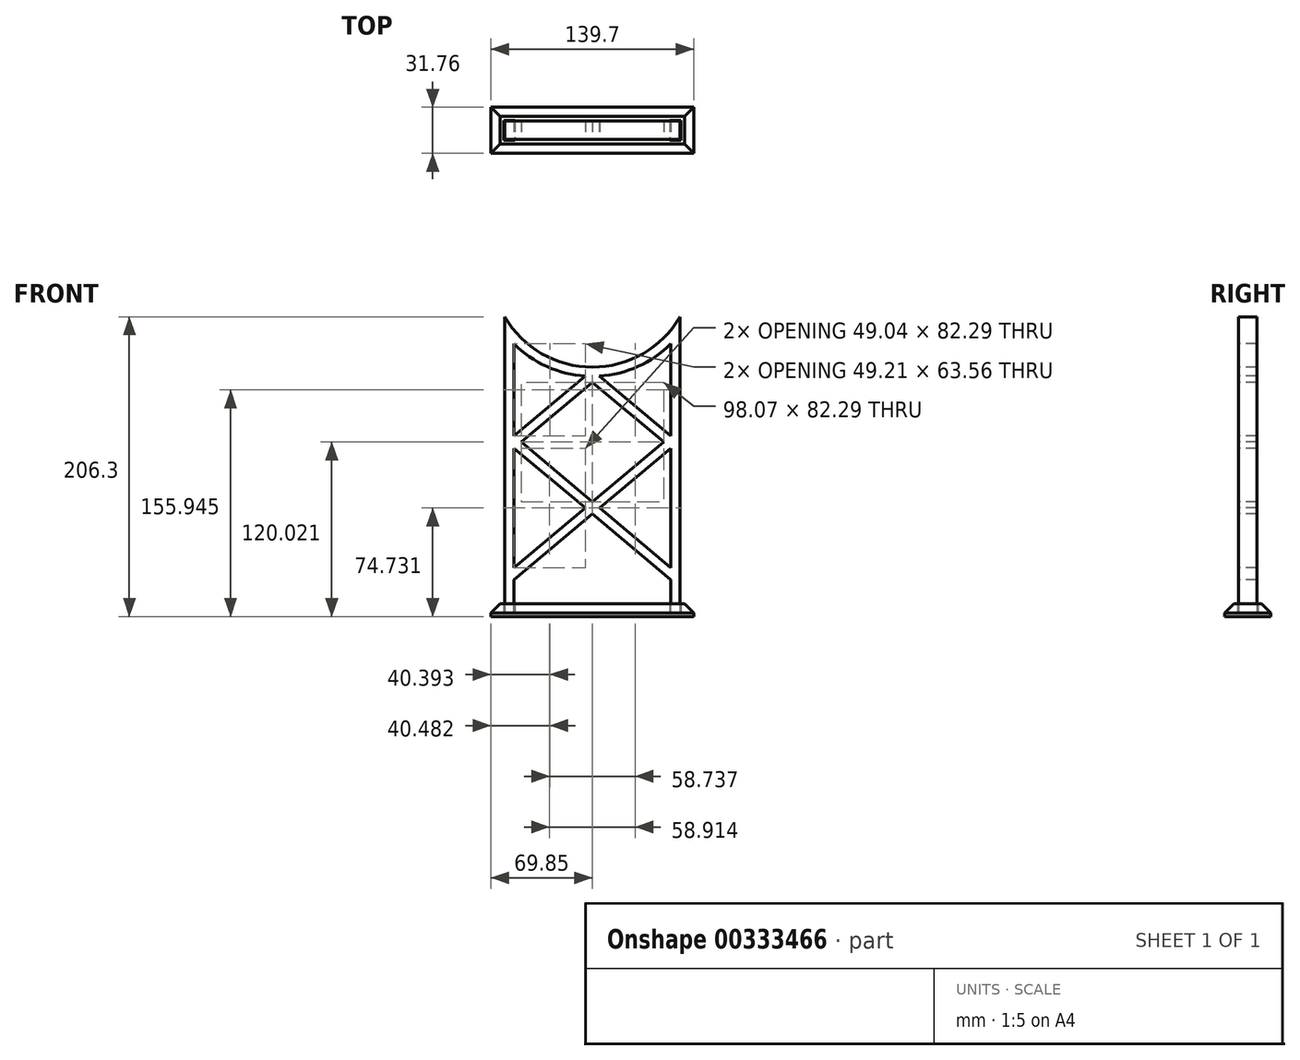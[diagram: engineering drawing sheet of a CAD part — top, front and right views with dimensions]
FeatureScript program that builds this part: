
annotation { "Feature Type Name" : "Feature", "Feature Type Description" : "" }
export const myFeature = defineFeature(function(context is Context, id is Id, definition is map)
    precondition{}
    {
        {
            var Q0;
            Q0=qCreatedBy(makeId("Top.planeOp"),FACE);
            var sketch = newSketch(context, id + "F0", { "sketchPlane" : qUnion([Q0])});
            skLineSegment(sketch, "E0.bottom", {"start": v(60.33, -6.35) * mm, "end": v(-60.33, -6.35) * mm});
            skLineSegment(sketch, "E0.top", {"start": v(60.33, 6.35) * mm, "end": v(-60.33, 6.35) * mm});
            skLineSegment(sketch, "E0.left", {"start": v(60.33, -6.35) * mm, "end": v(60.33, 6.35) * mm});
            skLineSegment(sketch, "E0.right", {"start": v(-60.33, -6.35) * mm, "end": v(-60.33, 6.35) * mm});
            skPoint(sketch, "E0.middle", {"position": v(0, 0) * mm});
            skSolve(sketch);
        }
        {
            var Q0;
            Q0 = qSketchRegion(id + "F0", true);
            extrude(context, id + "F1", {"entities" : qUnion([Q0]), "depth" : 228.6 * mm});
        }
        {
            var Q0;
            Q0=qCreatedBy(makeId("Front.planeOp"),FACE);
            var sketch = newSketch(context, id + "F2", { "sketchPlane" : qUnion([Q0])});
            skLineSegment(sketch, "E1", {"start": v(0, 0) * mm, "end": v(0, 169.12) * mm, "construction": true});
            skLineSegment(sketch, "E2", {"start": v(0, 169.12) * mm, "end": v(0, 238.97) * mm, "construction": true});
            skCircle(sketch, "E3", {"center": v(0, 238.97) * mm, "radius": 69.85 * mm});
            skCircle(sketch, "E4", {"center": v(0, 238.97) * mm, "radius": 76.2 * mm, "construction": true});
            skLineSegment(sketch, "E5", {"start": v(0, 238.97) * mm, "end": v(-60.33, 192.42) * mm, "construction": true});
            skLineSegment(sketch, "E6", {"start": v(-60.33, 192.42) * mm, "end": v(60.33, 192.42) * mm, "construction": true});
            skLineSegment(sketch, "E7", {"start": v(60.33, 192.42) * mm, "end": v(0, 238.97) * mm, "construction": true});
            skArc(sketch, "E8", {"start": v(-60.33, 192.42) * mm, "mid": v(0, 162.77) * mm, "end": v(60.33, 192.42) * mm});
            skLineSegment(sketch, "E9", {"start": v(0, 238.97) * mm, "end": v(-60.33, 203.76) * mm, "construction": true});
            skLineSegment(sketch, "E10", {"start": v(-60.33, 203.76) * mm, "end": v(60.33, 203.76) * mm, "construction": true});
            skLineSegment(sketch, "E11", {"start": v(60.32, 203.76) * mm, "end": v(0, 238.97) * mm, "construction": true});
            skLineSegment(sketch, "E12", {"start": v(-60.33, 203.76) * mm, "end": v(-60.33, 192.42) * mm});
            skLineSegment(sketch, "E13", {"start": v(60.33, 203.76) * mm, "end": v(60.33, 192.42) * mm});
            skLineSegment(sketch, "E14", {"start": v(-60.33, 192.42) * mm, "end": v(-60.33, 0) * mm});
            skLineSegment(sketch, "E15", {"start": v(-60.33, 0) * mm, "end": v(60.32, 0) * mm});
            skLineSegment(sketch, "E16", {"start": v(60.33, 0) * mm, "end": v(60.33, 192.42) * mm});
            skLineSegment(sketch, "E17", {"start": v(-60.33, 0) * mm, "end": v(-53.97, 0) * mm});
            skLineSegment(sketch, "E18", {"start": v(-53.98, 0) * mm, "end": v(-53.98, 185.18) * mm});
            skLineSegment(sketch, "E19", {"start": v(60.32, 0) * mm, "end": v(53.98, 0) * mm});
            skLineSegment(sketch, "E20", {"start": v(53.98, 0) * mm, "end": v(53.98, 185.18) * mm});
            skLineSegment(sketch, "E21", {"start": v(0, 0) * mm, "end": v(0, 162.77) * mm, "construction": true});
            skLineSegment(sketch, "E22", {"start": v(0, 162.77) * mm, "end": v(-53.97, 117.48) * mm, "construction": true});
            skLineSegment(sketch, "E23", {"start": v(-53.98, 117.48) * mm, "end": v(0, 72.2) * mm, "construction": true});
            skLineSegment(sketch, "E24", {"start": v(0, 72.2) * mm, "end": v(-53.97, 26.9) * mm, "construction": true});
            skLineSegment(sketch, "E25", {"start": v(0, 162.77) * mm, "end": v(53.98, 117.48) * mm, "construction": true});
            skLineSegment(sketch, "E26", {"start": v(53.98, 117.48) * mm, "end": v(0, 72.2) * mm, "construction": true});
            skLineSegment(sketch, "E27", {"start": v(0, 72.2) * mm, "end": v(53.97, 26.9) * mm, "construction": true});
            skLineSegment(sketch, "E28", {"start": v(53.98, 26.9) * mm, "end": v(-53.97, 26.9) * mm, "construction": true});
            skLineSegment(sketch, "E29", {"start": v(-53.97, 117.48) * mm, "end": v(53.98, 117.48) * mm, "construction": true});
            skLineSegment(sketch, "E30", {"start": v(-4.76, 162.92) * mm, "end": v(-53.97, 121.63) * mm});
            skLineSegment(sketch, "E31", {"start": v(0, 158.63) * mm, "end": v(-53.97, 113.34) * mm});
            skLineSegment(sketch, "E32", {"start": v(0, 158.63) * mm, "end": v(53.98, 113.34) * mm});
            skLineSegment(sketch, "E33", {"start": v(-10.57, 158.05) * mm, "end": v(-8.53, 155.61) * mm, "construction": true});
            skLineSegment(sketch, "E34", {"start": v(-8.53, 155.61) * mm, "end": v(-6.49, 153.18) * mm, "construction": true});
            skLineSegment(sketch, "E35", {"start": v(3.6, 155.61) * mm, "end": v(5.63, 158.05) * mm, "construction": true});
            skLineSegment(sketch, "E36", {"start": v(4.76, 162.92) * mm, "end": v(53.98, 121.63) * mm});
            skLineSegment(sketch, "E37", {"start": v(5.63, 158.05) * mm, "end": v(7.67, 160.48) * mm, "construction": true});
            skLineSegment(sketch, "E38", {"start": v(0, 76.34) * mm, "end": v(-53.98, 121.63) * mm});
            skLineSegment(sketch, "E39", {"start": v(0, 68.05) * mm, "end": v(-53.98, 113.34) * mm});
            skLineSegment(sketch, "E40", {"start": v(0, 76.34) * mm, "end": v(53.98, 121.63) * mm});
            skLineSegment(sketch, "E41", {"start": v(0, 68.05) * mm, "end": v(53.98, 113.34) * mm});
            skLineSegment(sketch, "E42", {"start": v(-27.08, 90.77) * mm, "end": v(-25.04, 93.2) * mm, "construction": true});
            skLineSegment(sketch, "E43", {"start": v(-25.04, 93.2) * mm, "end": v(-23, 95.64) * mm, "construction": true});
            skLineSegment(sketch, "E44", {"start": v(15.14, 89.04) * mm, "end": v(17.18, 86.6) * mm, "construction": true});
            skLineSegment(sketch, "E45", {"start": v(17.18, 86.6) * mm, "end": v(19.22, 84.17) * mm, "construction": true});
            skLineSegment(sketch, "E46", {"start": v(0, 76.34) * mm, "end": v(-53.98, 31.05) * mm});
            skLineSegment(sketch, "E47", {"start": v(0, 68.05) * mm, "end": v(-53.98, 22.76) * mm});
            skLineSegment(sketch, "E48", {"start": v(0, 76.34) * mm, "end": v(53.98, 31.05) * mm});
            skLineSegment(sketch, "E49", {"start": v(0, 68.05) * mm, "end": v(53.98, 22.76) * mm});
            skLineSegment(sketch, "E50", {"start": v(-34.53, 47.36) * mm, "end": v(-32.49, 44.93) * mm, "construction": true});
            skLineSegment(sketch, "E51", {"start": v(-32.49, 44.93) * mm, "end": v(-30.45, 42.5) * mm, "construction": true});
            skLineSegment(sketch, "E52", {"start": v(12.8, 57.3) * mm, "end": v(14.85, 59.73) * mm, "construction": true});
            skLineSegment(sketch, "E53", {"start": v(14.85, 59.73) * mm, "end": v(16.9, 62.16) * mm, "construction": true});
            skSolve(sketch);
        }
        {
            var Q0;
            {var subQ0=sQuery(id+"F2.wireOp",EDGE,"E3");var subQ1=makeQuery(id+"F2.imprint","INTERSECT",VERTEX,{"derivedFrom":[subQ0,sQuery(id+"F2.wireOp",EDGE,"E12")]});Q0=makeQuery(id+"F2.imprint","IMPRINT",FACE,{"disambiguationData":[TD([[makeQuery(id+"F2.imprint","IMPRINT",EDGE,{"disambiguationData":[TD([[subQ1,-1.0]])],"derivedFrom":subQ0}),1.0]])]});}
            var Q1;
            {var subQ3=sQuery(id+"F2.wireOp",EDGE,"E30");Q1=makeQuery(id+"F2.imprint","IMPRINT",FACE,{"disambiguationData":[TD([[makeQuery(id+"F2.imprint","IMPRINT",EDGE,{"derivedFrom":subQ3}),-1.0]])]});}
            var Q2;
            {var subQ3=sQuery(id+"F2.wireOp",EDGE,"E36");Q2=makeQuery(id+"F2.imprint","IMPRINT",FACE,{"disambiguationData":[TD([[makeQuery(id+"F2.imprint","IMPRINT",EDGE,{"derivedFrom":subQ3}),1.0]])]});}
            var Q3;
            {var subQ0=sQuery(id+"F2.wireOp",EDGE,"E32");var subQ1=sQuery(id+"F2.wireOp",EDGE,"E31");var subQ2=makeQuery(id+"F2.imprint","INTERSECT",VERTEX,{"derivedFrom":[subQ1,subQ0]});Q3=makeQuery(id+"F2.imprint","IMPRINT",FACE,{"disambiguationData":[TD([[makeQuery(id+"F2.imprint","IMPRINT",EDGE,{"disambiguationData":[TD([[subQ2,-1.0]])],"derivedFrom":subQ1}),1.0]])]});}
            var Q4;
            {var subQ1=sQuery(id+"F2.wireOp",EDGE,"E18");var subQ3=sQuery(id+"F2.wireOp",EDGE,"E46");var subQ4=makeQuery(id+"F2.imprint","INTERSECT",VERTEX,{"derivedFrom":[subQ1,subQ3]});Q4=makeQuery(id+"F2.imprint","IMPRINT",FACE,{"disambiguationData":[TD([[makeQuery(id+"F2.imprint","IMPRINT",EDGE,{"disambiguationData":[TD([[subQ4,1.0]])],"derivedFrom":subQ3}),-1.0]])]});}
            var Q5;
            {var subQ1=sQuery(id+"F2.wireOp",EDGE,"E20");var subQ3=sQuery(id+"F2.wireOp",EDGE,"E48");var subQ4=makeQuery(id+"F2.imprint","INTERSECT",VERTEX,{"derivedFrom":[subQ1,subQ3]});Q5=makeQuery(id+"F2.imprint","IMPRINT",FACE,{"disambiguationData":[TD([[makeQuery(id+"F2.imprint","IMPRINT",EDGE,{"disambiguationData":[TD([[subQ4,1.0]])],"derivedFrom":subQ3}),1.0]])]});}
            var Q6;
            {var subQ1=sQuery(id+"F2.wireOp",EDGE,"E15");Q6=makeQuery(id+"F2.imprint","IMPRINT",FACE,{"disambiguationData":[TD([[makeQuery(id+"F2.imprint","IMPRINT",EDGE,{"derivedFrom":subQ1}),1.0]])]});}
            extrude(context, id + "F3", {"entities" : qUnion([Q0, Q1, Q2, Q3, Q4, Q5, Q6]), "operationType" : NewBodyOperationType.REMOVE, "oppositeDirection" : true, "depth" : 25.4 * mm, "hasSecondDirection" : true, "secondDirectionOppositeDirection" : false, "secondDirectionDepth" : 25.4 * mm});
        }
        {
            var Q0;
            Q0=qCreatedBy(makeId("Top.planeOp"),FACE);
            var sketch = newSketch(context, id + "F4", { "sketchPlane" : qUnion([Q0])});
            skLineSegment(sketch, "E54.bottom", {"start": v(-69.85, 15.87) * mm, "end": v(69.85, 15.87) * mm});
            skLineSegment(sketch, "E54.top", {"start": v(-69.85, -15.87) * mm, "end": v(69.85, -15.87) * mm});
            skLineSegment(sketch, "E54.left", {"start": v(-69.85, 15.88) * mm, "end": v(-69.85, -15.87) * mm});
            skLineSegment(sketch, "E54.right", {"start": v(69.85, 15.88) * mm, "end": v(69.85, -15.87) * mm});
            skPoint(sketch, "E54.middle", {"position": v(0, 0) * mm});
            skLineSegment(sketch, "E55", {"start": v(0, 0) * mm, "end": v(-57.15, 0) * mm, "construction": true});
            skLineSegment(sketch, "E56", {"start": v(0, 0) * mm, "end": v(57.15, 0) * mm, "construction": true});
            skLineSegment(sketch, "E57.bottom", {"start": v(-60.83, 6.86) * mm, "end": v(-53.47, 6.86) * mm});
            skLineSegment(sketch, "E57.top", {"start": v(-60.83, -6.86) * mm, "end": v(-53.47, -6.86) * mm});
            skLineSegment(sketch, "E57.left", {"start": v(-60.83, 6.86) * mm, "end": v(-60.83, -6.86) * mm});
            skLineSegment(sketch, "E57.right", {"start": v(-53.47, 6.86) * mm, "end": v(-53.47, -6.86) * mm});
            skPoint(sketch, "E57.middle", {"position": v(-57.15, 0) * mm});
            skLineSegment(sketch, "E58.bottom", {"start": v(53.47, 6.86) * mm, "end": v(60.83, 6.86) * mm});
            skLineSegment(sketch, "E58.top", {"start": v(53.47, -6.86) * mm, "end": v(60.83, -6.86) * mm});
            skLineSegment(sketch, "E58.left", {"start": v(53.47, 6.86) * mm, "end": v(53.47, -6.86) * mm});
            skLineSegment(sketch, "E58.right", {"start": v(60.83, 6.86) * mm, "end": v(60.83, -6.86) * mm});
            skPoint(sketch, "E58.middle", {"position": v(57.15, 0) * mm});
            skSolve(sketch);
        }
        {
            var Q0;
            Q0 = qSketchRegion(id + "F4", true);
            extrude(context, id + "F5", {"entities" : qUnion([Q0]), "depth" : 6.35 * mm});
        }
        {
            var Q0;
            Q0=makeQuery(id+"F5.opExtrude","CAP_EDGE",EDGE,{"disambiguationData":[OSD([sQuery(id+"F4.wireOp",EDGE,"E54.top")])],"isStart":false});
            var Q1;
            Q1=makeQuery(id+"F5.opExtrude","CAP_EDGE",EDGE,{"disambiguationData":[OSD([sQuery(id+"F4.wireOp",EDGE,"E54.left")])],"isStart":false});
            var Q2;
            Q2=makeQuery(id+"F5.opExtrude","CAP_EDGE",EDGE,{"disambiguationData":[OSD([sQuery(id+"F4.wireOp",EDGE,"E54.bottom")])],"isStart":false});
            var Q3;
            Q3=makeQuery(id+"F5.opExtrude","CAP_EDGE",EDGE,{"disambiguationData":[OSD([sQuery(id+"F4.wireOp",EDGE,"E54.right")])],"isStart":false});
            chamfer(context, id + "F6", {"entities" : qUnion([Q0, Q1, Q2, Q3]), "width" : 6.35 * mm, "tangentPropagation" : true});
        }
        {
            var Q0;
            Q0=makeQuery(id+"F4.imprint","IMPRINT",FACE,{"disambiguationData":[TD([[makeQuery(id+"F4.imprint","IMPRINT",EDGE,{"derivedFrom":sQuery(id+"F4.wireOp",EDGE,"E54.bottom")}),-1.0]])]});
            var Q1;
            Q1=makeQuery(id+"F4.imprint","IMPRINT",FACE,{"disambiguationData":[TD([[makeQuery(id+"F4.imprint","IMPRINT",EDGE,{"derivedFrom":sQuery(id+"F4.wireOp",EDGE,"E57.bottom")}),-1.0]])]});
            var Q2;
            Q2=makeQuery(id+"F4.imprint","IMPRINT",FACE,{"disambiguationData":[TD([[makeQuery(id+"F4.imprint","IMPRINT",EDGE,{"derivedFrom":sQuery(id+"F4.wireOp",EDGE,"E58.bottom")}),-1.0]])]});
            extrude(context, id + "F7", {"entities" : qUnion([Q0, Q1, Q2]), "operationType" : NewBodyOperationType.ADD, "oppositeDirection" : true, "depth" : 2.54 * mm, "offsetDistance" : 25.4 * mm});
        }
    });
